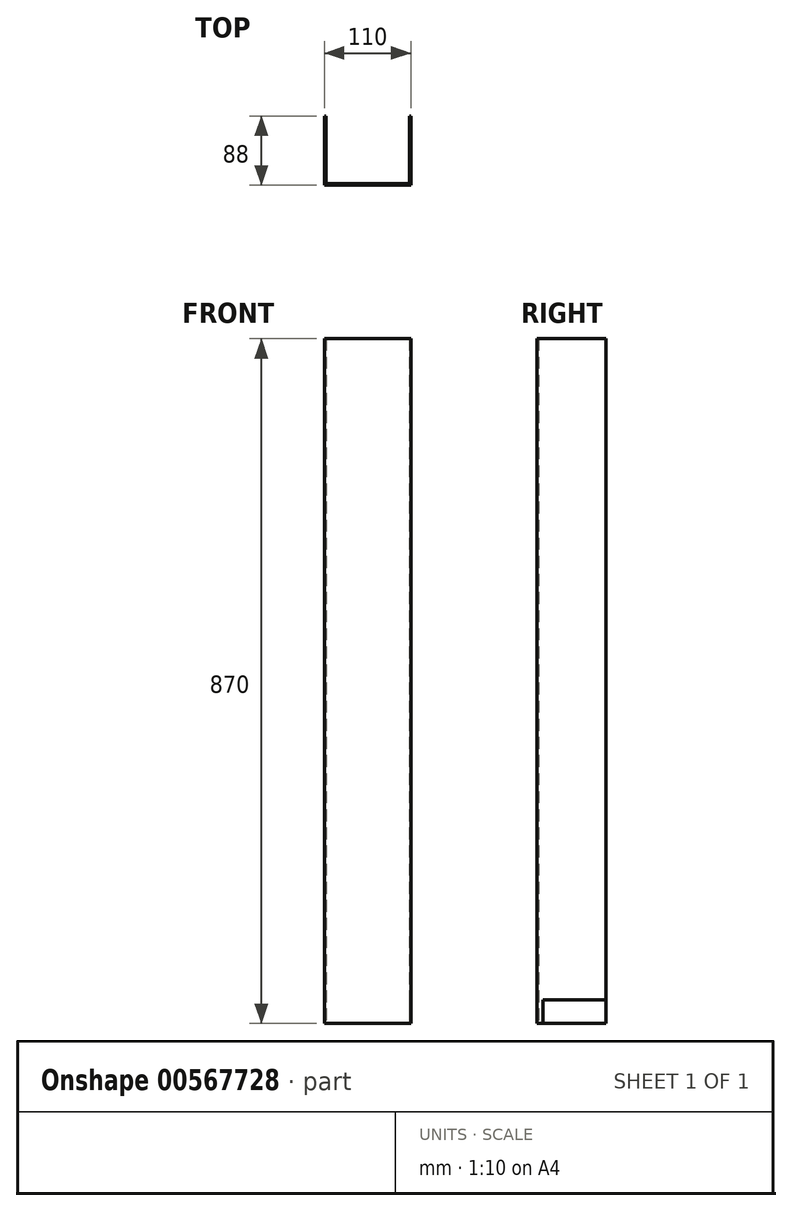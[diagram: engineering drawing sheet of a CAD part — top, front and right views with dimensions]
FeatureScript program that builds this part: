
annotation { "Feature Type Name" : "Feature", "Feature Type Description" : "" }
export const myFeature = defineFeature(function(context is Context, id is Id, definition is map)
    precondition{}
    {
        {
            var Q0;
            Q0=qCreatedBy(makeId("Top.planeOp"),FACE);
            var sketch = newSketch(context, id + "F0", { "sketchPlane" : qUnion([Q0])});
            skLineSegment(sketch, "E0", {"start": v(0, 0) * mm, "end": v(0, -88) * mm});
            skLineSegment(sketch, "E1", {"start": v(0, -88) * mm, "end": v(110, -88) * mm});
            skLineSegment(sketch, "E2", {"start": v(110, -88) * mm, "end": v(110, 0) * mm});
            skLineSegment(sketch, "E3", {"start": v(110, 0) * mm, "end": v(108, 0) * mm});
            skLineSegment(sketch, "E4", {"start": v(108, 0) * mm, "end": v(108, -86) * mm});
            skLineSegment(sketch, "E5", {"start": v(108, -86) * mm, "end": v(2, -86) * mm});
            skLineSegment(sketch, "E6", {"start": v(2, -86) * mm, "end": v(2, 0) * mm});
            skLineSegment(sketch, "E7", {"start": v(2, 0) * mm, "end": v(0, 0) * mm});
            skSolve(sketch);
        }
        {
            var Q0;
            Q0 = qSketchRegion(id + "F0", true);
            extrude(context, id + "F1", {"entities" : qUnion([Q0]), "depth" : 870 * mm, "offsetDistance" : 25 * mm});
        }
        {
            var Q0;
            Q0=makeQuery(id+"F1.opExtrude","SWEPT_FACE",FACE,{"disambiguationData":[OSD([sQuery(id+"F0.wireOp",EDGE,"E2")])]});
            var sketch = newSketch(context, id + "F2", { "sketchPlane" : qUnion([Q0])});
            skLineSegment(sketch, "E8", {"start": v(-80, 0) * mm, "end": v(-80, 30) * mm});
            skLineSegment(sketch, "E9", {"start": v(-80, 30) * mm, "end": v(0, 30) * mm});
            skSolve(sketch);
        }
        {
            var Q0;
            Q0 = qSketchRegion(id + "F2", true);
            var Q1;
            {var subQ0=sQuery(id+"F2.wireOp",EDGE,"E8");Q1=makeQuery(id+"F2.imprint","IMPRINT",FACE,{"disambiguationData":[TD([[makeQuery(id+"F2.imprint","IMPRINT",EDGE,{"derivedFrom":subQ0}),-1.0]])]});}
            extrude(context, id + "F3", {"entities" : qUnion([Q0, Q1]), "operationType" : NewBodyOperationType.REMOVE, "endBound" : BoundingType.UP_TO_NEXT, "oppositeDirection" : true, "depth" : 25 * mm, "offsetDistance" : 25 * mm});
        }
    });
